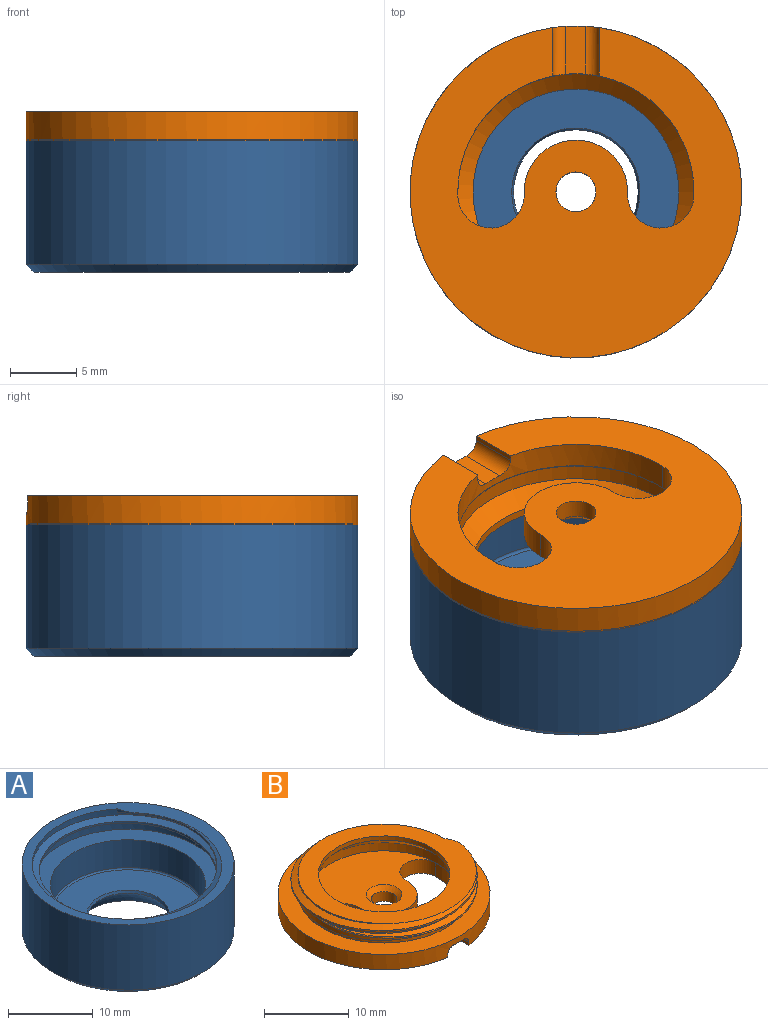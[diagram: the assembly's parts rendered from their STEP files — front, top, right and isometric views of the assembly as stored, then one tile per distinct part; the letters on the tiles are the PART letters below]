
ASSEMBLY  parts=2 mates=1
PART A: 20 faces, bbox 25.3x26.1x10.8 mm
  f0: cylinder r=11.3mm len=22.6mm, axis (0,0,1), area 74.3mm2, adj f1,f2,f3,f5,f13,f14,f15,f17
  f1: bspline ~25.82x24.29mm, area 73.8mm2, adj f0,f15,f16,f17,f18
  f2: bspline ~25.82x24.32mm, area 71.3mm2, adj f0,f5,f16,f18
  f3: plane 22.6x22.6mm, normal (0,0,1), area 138.2mm2, adj f0,f7,f13,f14
  f4: cylinder r=12.5mm len=25mm, axis (0,0,-1), area 738.3mm2, adj f5,f11
  f5: plane 25.02x25.02mm, normal (0,0,1), area 102mm2, adj f0,f2,f4,f16,f17
  f6: plane 23.8x23.8mm, normal (0,0,-1), area 306.6mm2, adj f11,f12
  f7: cylinder r=9.15mm len=18.3mm, axis (0,0,1), area 230mm2, adj f3,f19
  f8: plane 17.9x17.9mm, normal (0,0,1), area 178.4mm2, adj f10,f19
  f9: sphere r=7mm, area 99.8mm2, adj f10,f12
  f10: cone r=4.69mm half-angle=21deg, axis (0,0,1), area 11.4mm2, adj f8,f9
  f11: cone r=12.5mm half-angle=45deg, axis (0,0,1), area 65mm2, adj f4,f6
  f12: cone r=6.63mm half-angle=57.4deg, axis (0,0,-1), area 13.3mm2, adj f6,f9
  f13: extruded ~22.6x19.94mm, area 45.3mm2, adj f0,f3,f14,f15
  f14: extruded ~1x0.14mm, area 0.2mm2, adj f0,f3,f13
  f15: plane 17.65x16.34mm, normal (0,0,-1), area 9.3mm2, adj f0,f1,f13,f18
  f16: bspline ~21.38x21.37mm, area 20.1mm2, adj f1,f2,f5,f17,f18
  f17: bspline ~2.18x1.04mm, area 0.6mm2, adj f0,f1,f5,f16
  f18: bspline ~18.73x6.07mm, area 9.3mm2, adj f0,f1,f2,f15,f16
  f19: torus R=8.95mm, axis (0,0,1), area 17.9mm2, adj f7,f8
PART B: 28 faces, bbox 25.4x26.4x5.9 mm
  f0: cylinder r=12.5mm len=25mm, axis (0,0,1), area 168.3mm2, adj f2,f8,f21,f22,f23,f24,f25
  f1: cylinder r=8.9mm len=17.8mm, axis (0,0,1), area 52.7mm2, adj f2,f6,f12,f13,f21,f22,f23,f24
  f2: plane 25x24.88mm, normal (0,0,-1), area 348.7mm2, adj f0,f1,f10,f11,f12,f13,f22,f23
  f3: bspline ~9.74x6.18mm, area 0mm2, adj f5,f15
  f4: bspline ~25.98x22.5mm, area 69.2mm2, adj f5,f7,f15,f17,f18
  f5: cylinder r=10.15mm len=20.3mm, axis (0,0,-1), area 79.8mm2, adj f3,f4,f7,f8,f14,f15,f16,f19
  f6: plane 17.9x17.9mm, normal (0,0,1), area 115.4mm2, adj f1,f9,f11,f12,f13,f20
  f7: plane 21.36x21.08mm, normal (0,0,1), area 146.4mm2, adj f4,f5,f17,f19,f26
  f8: plane 25.02x25.02mm, normal (0,0,1), area 167.2mm2, adj f0,f5
  f9: cylinder r=8.95mm len=17.9mm, axis (0,0,1), area 67.5mm2, adj f6,f27
  f10: cylinder r=1.5mm len=3mm, axis (0,0,1), area 13.2mm2, adj f2,f20
  f11: cylinder r=3.9mm len=7.8mm, axis (0,0,1), area 25.1mm2, adj f2,f6,f12,f13
  f12: cylinder r=2.5mm len=5mm, axis (0,0,1), area 15.7mm2, adj f1,f2,f6,f11
  f13: cylinder r=2.5mm len=5mm, axis (0,0,1), area 15.7mm2, adj f1,f2,f6,f11
  f14: bspline ~25.98x22.5mm, area 63mm2, adj f5,f16,f17,f19
  f15: extruded ~20.3x18.01mm, area 22.1mm2, adj f3,f4,f5,f16,f18
  f16: plane 21.08x15.79mm, normal (0,0,-1), area 16.1mm2, adj f5,f14,f15,f17,f18
  f17: bspline ~22.38x22.18mm, area 20.6mm2, adj f4,f7,f14,f16,f18,f19
  f18: bspline ~13.73x13.08mm, area 5.4mm2, adj f4,f15,f16,f17
  f19: bspline ~2.53x1.03mm, area 0.7mm2, adj f5,f7,f14,f17
  f20: cone r=1.5mm half-angle=45deg, axis (0,0,1), area 9.6mm2, adj f6,f10
  f21: plane 3.63x1.5mm, normal (0,0,-1), area 5.4mm2, adj f0,f1,f24,f25
  f22: plane 3.65x0.4mm, normal (-1,0,0), area 1.5mm2, adj f0,f1,f2,f25
  f23: plane 3.65x0.4mm, normal (1,0,0), area 1.5mm2, adj f0,f1,f2,f24
  f24: cylinder r=1mm len=3.75mm, axis (0,1,0), area 5.7mm2, adj f0,f1,f21,f23
  f25: cylinder r=1mm len=3.75mm, axis (0,-1,0), area 5.7mm2, adj f0,f1,f21,f22
  f26: cylinder r=7.75mm len=15.5mm, axis (0,0,1), area 29.2mm2, adj f7,f27
  f27: cone r=8.95mm half-angle=45deg, axis (0,0,-1), area 89mm2, adj f9,f26
PLACE A t=(-5.82,0.55,0.87)mm
PLACE B rot(axis=(1,0,0),180deg) t=(-5.82,0.55,10.77)mm
MATE cylindrical B.f0 <-> A.f0  axis (0,0,1) through (-5.82,0.55,9.37)mm
